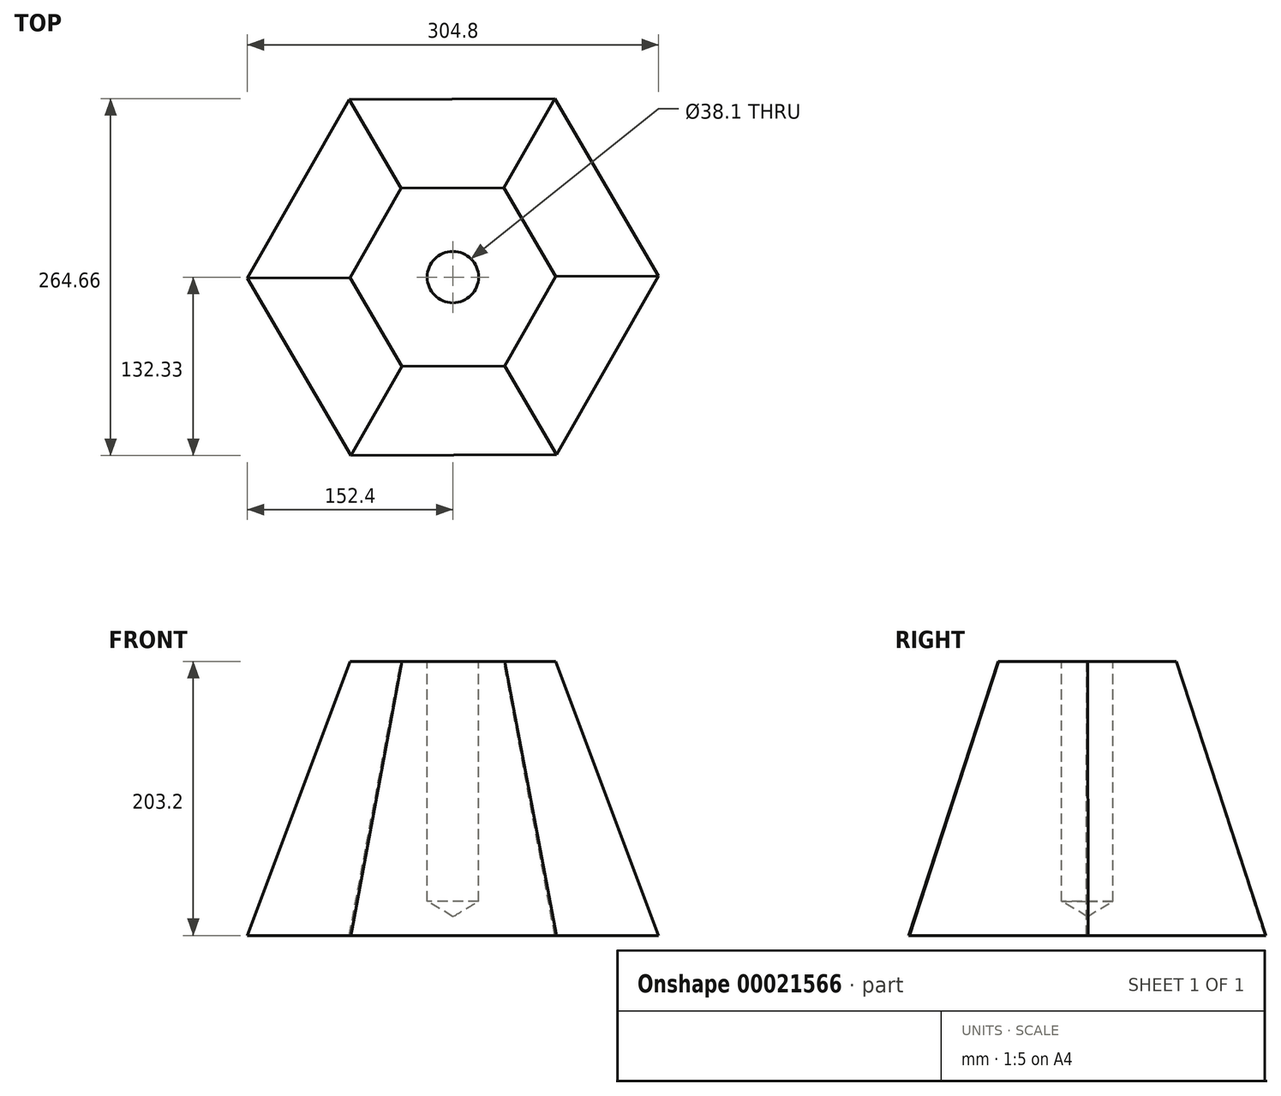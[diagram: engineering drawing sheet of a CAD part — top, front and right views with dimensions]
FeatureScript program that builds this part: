
annotation { "Feature Type Name" : "Feature", "Feature Type Description" : "" }
export const myFeature = defineFeature(function(context is Context, id is Id, definition is map)
    precondition{}
    {
        {
            var Q0;
            Q0=qCreatedBy(makeId("Top.planeOp"),FACE);
            cPlane(context, id + "F0", {"entities" : qUnion([Q0]), "cplaneType" : CPlaneType.OFFSET, "offset" : 203.2 * mm, "width" : 152.4 * mm, "height" : 152.4 * mm});
        }
        {
            var Q0;
            Q0=qCreatedBy(makeId("Top.planeOp"),FACE);
            var sketch = newSketch(context, id + "F1", { "sketchPlane" : qUnion([Q0])});
            skCircle(sketch, "E0.cCircle", {"center": v(0, 0) * mm, "radius": 131.98 * mm, "construction": true});
            skLineSegment(sketch, "E0.0", {"start": v(75.6, 132.33) * mm, "end": v(152.4, 0.7) * mm});
            skLineSegment(sketch, "E0.1", {"start": v(152.4, 0.7) * mm, "end": v(76.8, -131.63) * mm});
            skLineSegment(sketch, "E0.2", {"start": v(76.8, -131.63) * mm, "end": v(-75.6, -132.33) * mm});
            skLineSegment(sketch, "E0.3", {"start": v(-75.6, -132.33) * mm, "end": v(-152.4, -0.7) * mm});
            skLineSegment(sketch, "E0.4", {"start": v(-152.4, -0.7) * mm, "end": v(-76.8, 131.63) * mm});
            skLineSegment(sketch, "E0.5", {"start": v(-76.8, 131.63) * mm, "end": v(75.6, 132.33) * mm});
            skPoint(sketch, "E0.0.midPoint", {"position": v(114, 66.52) * mm});
            skSolve(sketch);
        }
        {
            var Q0;
            Q0=qCreatedBy(id+"F0.planeOp",FACE);
            var sketch = newSketch(context, id + "F2", { "sketchPlane" : qUnion([Q0])});
            skCircle(sketch, "E1.cCircle", {"center": v(0, 0) * mm, "radius": 66 * mm, "construction": true});
            skLineSegment(sketch, "E1.0", {"start": v(37.8, 66.16) * mm, "end": v(76.2, 0.34) * mm});
            skLineSegment(sketch, "E1.1", {"start": v(76.2, 0.34) * mm, "end": v(38.4, -65.82) * mm});
            skLineSegment(sketch, "E1.2", {"start": v(38.4, -65.82) * mm, "end": v(-37.8, -66.16) * mm});
            skLineSegment(sketch, "E1.3", {"start": v(-37.8, -66.16) * mm, "end": v(-76.2, -0.34) * mm});
            skLineSegment(sketch, "E1.4", {"start": v(-76.2, -0.34) * mm, "end": v(-38.4, 65.82) * mm});
            skLineSegment(sketch, "E1.5", {"start": v(-38.4, 65.82) * mm, "end": v(37.8, 66.16) * mm});
            skPoint(sketch, "E1.0.midPoint", {"position": v(57, 33.25) * mm});
            skSolve(sketch);
        }
        {
            var Q0;
            Q0 = qSketchRegion(id + "F1", true);
            var Q1;
            Q1=makeQuery(id+"F2.imprint","IMPRINT",FACE,{"disambiguationData":[TD([[makeQuery(id+"F2.imprint","IMPRINT",EDGE,{"derivedFrom":sQuery(id+"F2.wireOp",EDGE,"E1.0")}),-1.0]])]});
            loft(context, id + "F3", {"sheetProfilesArray" : [{ "sheetProfileEntities" : qUnion([Q0]) }, { "sheetProfileEntities" : qUnion([Q1]) }]});
        }
        {
            var Q0;
            Q0=makeQuery(id+"F3.opLoft","CAP_FACE",FACE,{"disambiguationData":[OSD([makeQuery(id+"F2.imprint","IMPRINT",FACE,{"disambiguationData":[TD([[makeQuery(id+"F2.imprint","IMPRINT",EDGE,{"derivedFrom":sQuery(id+"F2.wireOp",EDGE,"E1.0")}),-1.0]])]})])],"isStart":true});
            var sketch = newSketch(context, id + "F4", { "sketchPlane" : qUnion([Q0])});
            skCircle(sketch, "E2", {"center": v(0, 0) * mm, "radius": 19.05 * mm});
            skSolve(sketch);
        }
        {
            var Q0;
            Q0=sQuery(id+"F4.wireOp",VERTEX,"E2.center");
            var Q1;
            Q1=makeQuery(id+"F3.opLoft","SWEPT_BODY",BODY,{"disambiguationData":[OSD([makeQuery(id+"F1.imprint","IMPRINT",FACE,{"disambiguationData":[TD([[makeQuery(id+"F1.imprint","IMPRINT",EDGE,{"derivedFrom":sQuery(id+"F1.wireOp",EDGE,"E0.0")}),-1.0]])]}),makeQuery(id+"F2.imprint","IMPRINT",FACE,{"disambiguationData":[TD([[makeQuery(id+"F2.imprint","IMPRINT",EDGE,{"derivedFrom":sQuery(id+"F2.wireOp",EDGE,"E1.0")}),-1.0]])]})])]});
            hole(context, id + "F5", {"style" : HoleStyle.SIMPLE, "holeDiameter" : 38.1 * mm, "endStyle" : HoleEndStyle.BLIND, "holeDepth" : 177.8 * mm, "locations" : qUnion([Q0]), "scope" : qUnion([Q1])});
        }
    });
